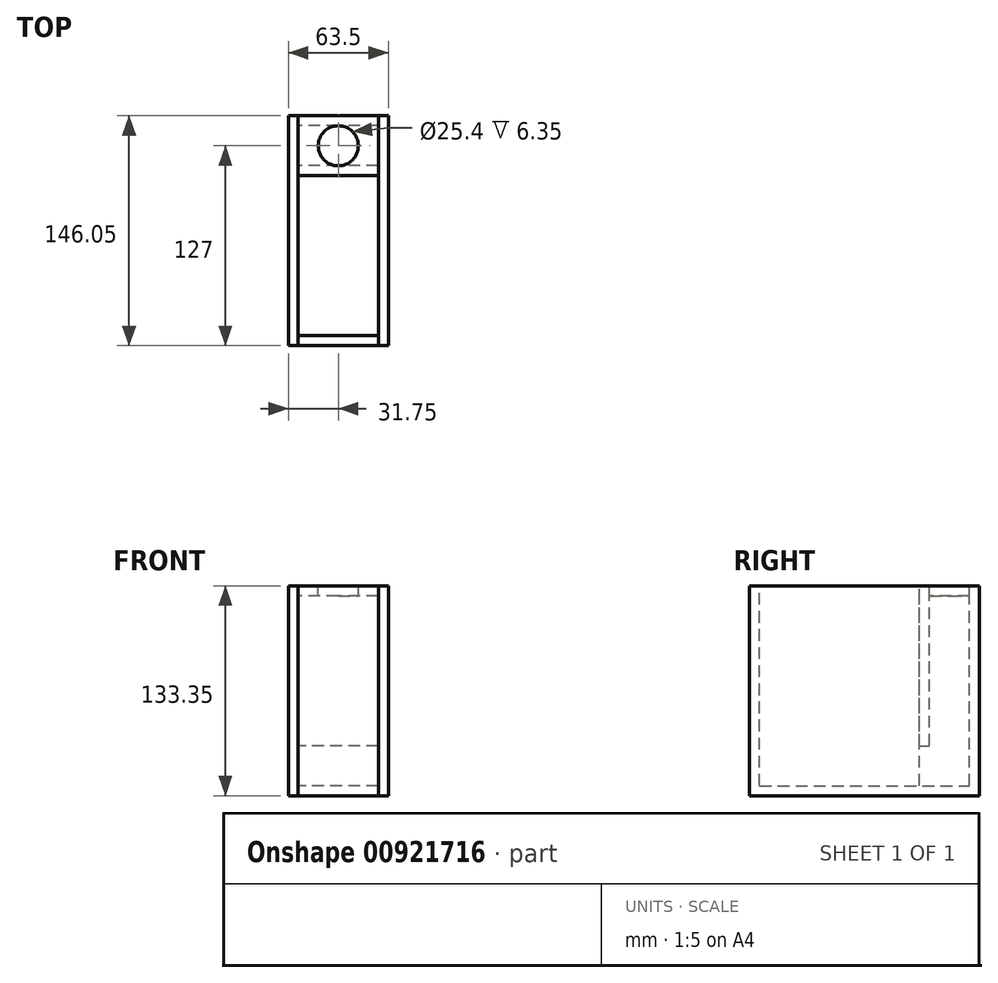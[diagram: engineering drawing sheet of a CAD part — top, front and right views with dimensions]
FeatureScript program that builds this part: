
annotation { "Feature Type Name" : "Feature", "Feature Type Description" : "" }
export const myFeature = defineFeature(function(context is Context, id is Id, definition is map)
    precondition{}
    {
        {
            var Q0;
            Q0=qCreatedBy(makeId("Right.planeOp"),FACE);
            var sketch = newSketch(context, id + "F0", { "sketchPlane" : qUnion([Q0])});
            skLineSegment(sketch, "E0.bottom", {"start": v(-50.8, 0) * mm, "end": v(50.8, 0) * mm});
            skLineSegment(sketch, "E0.top", {"start": v(-50.8, 127) * mm, "end": v(50.8, 127) * mm});
            skLineSegment(sketch, "E0.left", {"start": v(-50.8, 0) * mm, "end": v(-50.8, 127) * mm});
            skLineSegment(sketch, "E0.right", {"start": v(50.8, 0) * mm, "end": v(50.8, 127) * mm});
            skPoint(sketch, "E1", {"position": v(0, 0) * mm});
            skSolve(sketch);
        }
        {
            var Q0;
            Q0 = qSketchRegion(id + "F0", true);
            extrude(context, id + "F1", {"entities" : qUnion([Q0]), "oppositeDirection" : true, "depth" : 50.8 * mm, "offsetDistance" : 25.4 * mm});
        }
        {
            var Q0;
            Q0=makeQuery(id+"F1.opExtrude","CAP_FACE",FACE,{"disambiguationData":[OSD([sQuery(id+"F0.wireOp",EDGE,"E0.bottom"),sQuery(id+"F0.wireOp",EDGE,"E0.top"),sQuery(id+"F0.wireOp",EDGE,"E0.left"),sQuery(id+"F0.wireOp",EDGE,"E0.right")])],"isStart":false});
            var sketch = newSketch(context, id + "F2", { "sketchPlane" : qUnion([Q0])});
            skLineSegment(sketch, "E2", {"start": v(50.8, 0) * mm, "end": v(-82.55, 0) * mm});
            skLineSegment(sketch, "E3", {"start": v(-82.55, 0) * mm, "end": v(-82.55, 120.65) * mm});
            skLineSegment(sketch, "E4", {"start": v(-82.55, 120.65) * mm, "end": v(-50.8, 120.65) * mm});
            skLineSegment(sketch, "E5", {"start": v(-50.8, 120.65) * mm, "end": v(-50.8, 25.4) * mm});
            skLineSegment(sketch, "E6", {"start": v(-50.8, 25.4) * mm, "end": v(-57.15, 25.4) * mm});
            skLineSegment(sketch, "E7", {"start": v(-57.15, 25.4) * mm, "end": v(-57.15, 120.65) * mm});
            skLineSegment(sketch, "E8", {"start": v(-50.8, 120.65) * mm, "end": v(-50.8, 127) * mm});
            skLineSegment(sketch, "E9", {"start": v(-50.8, 127) * mm, "end": v(-82.55, 127) * mm});
            skLineSegment(sketch, "E10", {"start": v(-82.55, 127) * mm, "end": v(-88.9, 127) * mm});
            skLineSegment(sketch, "E11", {"start": v(-88.9, 127) * mm, "end": v(-88.9, 0) * mm});
            skLineSegment(sketch, "E12", {"start": v(-88.9, 0) * mm, "end": v(-88.9, -6.35) * mm});
            skLineSegment(sketch, "E13", {"start": v(-88.9, -6.35) * mm, "end": v(57.15, -6.35) * mm});
            skLineSegment(sketch, "E14", {"start": v(57.15, -6.35) * mm, "end": v(57.15, 127) * mm});
            skLineSegment(sketch, "E15", {"start": v(57.15, 127) * mm, "end": v(50.8, 127) * mm});
            skLineSegment(sketch, "E16", {"start": v(50.8, 127) * mm, "end": v(50.8, 0) * mm});
            skLineSegment(sketch, "E17", {"start": v(-57.15, 25.4) * mm, "end": v(-82.55, 0) * mm, "construction": true});
            skSolve(sketch);
        }
        {
            var Q0;
            Q0 = qSketchRegion(id + "F2", true);
            var Q1;
            Q1=makeQuery(id+"F2.imprint","IMPRINT",FACE,{"disambiguationData":[TD([[makeQuery(id+"F2.imprint","IMPRINT",EDGE,{"derivedFrom":sQuery(id+"F2.wireOp",EDGE,"A4J26bFV-rywj-hipJ-cBjO-Lqcr4Hk2ZQzP.bottom")}),1.0]])]});
            var Q2;
            Q2=makeQuery(id+"F1.opExtrude","CAP_FACE",FACE,{"disambiguationData":[OSD([sQuery(id+"F0.wireOp",EDGE,"E0.bottom"),sQuery(id+"F0.wireOp",EDGE,"E0.top"),sQuery(id+"F0.wireOp",EDGE,"E0.left"),sQuery(id+"F0.wireOp",EDGE,"E0.right")])],"isStart":true});
            extrude(context, id + "F3", {"entities" : qUnion([Q0, Q1]), "endBound" : BoundingType.UP_TO_SURFACE, "oppositeDirection" : true, "depth" : 25.4 * mm, "endBoundEntityFace" : qUnion([Q2]), "offsetDistance" : 25.4 * mm});
        }
        {
            var Q0;
            Q0=makeQuery(id+"F3.opExtrude","CAP_FACE",FACE,{"disambiguationData":[OSD([sQuery(id+"F2.wireOp",EDGE,"E2"),sQuery(id+"F2.wireOp",EDGE,"E3"),sQuery(id+"F2.wireOp",EDGE,"E4"),sQuery(id+"F2.wireOp",EDGE,"E5"),sQuery(id+"F2.wireOp",EDGE,"E6"),sQuery(id+"F2.wireOp",EDGE,"E7"),sQuery(id+"F2.wireOp",EDGE,"E8"),sQuery(id+"F2.wireOp",EDGE,"E9"),sQuery(id+"F2.wireOp",EDGE,"E10"),sQuery(id+"F2.wireOp",EDGE,"E11"),sQuery(id+"F2.wireOp",EDGE,"E12"),sQuery(id+"F2.wireOp",EDGE,"E13"),sQuery(id+"F2.wireOp",EDGE,"E14"),sQuery(id+"F2.wireOp",EDGE,"E15"),sQuery(id+"F2.wireOp",EDGE,"E16")])],"isStart":true});
            var sketch = newSketch(context, id + "F4", { "sketchPlane" : qUnion([Q0])});
            skLineSegment(sketch, "E18.bottom", {"start": v(-88.9, 127) * mm, "end": v(57.15, 127) * mm});
            skLineSegment(sketch, "E18.top", {"start": v(-88.9, -6.35) * mm, "end": v(57.15, -6.35) * mm});
            skLineSegment(sketch, "E18.left", {"start": v(-88.9, 127) * mm, "end": v(-88.9, -6.35) * mm});
            skLineSegment(sketch, "E18.right", {"start": v(57.15, 127) * mm, "end": v(57.15, -6.35) * mm});
            skSolve(sketch);
        }
        {
            var Q0;
            Q0 = qSketchRegion(id + "F4", true);
            var Q1;
            {var subQ1=sQuery(id+"F2.wireOp",EDGE,"OunrTzoC-Ow74-cI66-Frwy-KkpsYNKgRBLo.left");Q1=makeQuery(id+"F4.imprint","IMPRINT",FACE,{"disambiguationData":[TD([[makeQuery(id+"F4.imprint","IMPRINT",EDGE,{"derivedFrom":makeQuery(id+"F3.opExtrude","CAP_EDGE",EDGE,{"disambiguationData":[OSD([subQ1])],"isStart":false})}),1.0]])]});}
            var Q2;
            {var subQ4=sQuery(id+"F2.wireOp",EDGE,"OunrTzoC-Ow74-cI66-Frwy-KkpsYNKgRBLo.left");Q2=makeQuery(id+"F4.imprint","IMPRINT",FACE,{"disambiguationData":[TD([[makeQuery(id+"F4.imprint","IMPRINT",EDGE,{"derivedFrom":makeQuery(id+"F3.opExtrude","CAP_EDGE",EDGE,{"disambiguationData":[OSD([subQ4])],"isStart":false})}),-1.0]])]});}
            extrude(context, id + "F5", {"entities" : qUnion([Q0, Q1, Q2]), "depth" : 6.35 * mm, "offsetDistance" : 25.4 * mm});
        }
        {
            var Q0;
            Q0=makeQuery(id+"F3.opExtrude","SWEPT_EDGE",EDGE,{"disambiguationData":[OSD([sQuery(id+"F2.wireOp",EDGE,"E14"),sQuery(id+"F2.wireOp",EDGE,"E15")])]});
            cPoint(context, id + "F6", {"entities" : qUnion([Q0]), "parameter" : 0.5});
        }
        {
            var Q0;
            Q0 = qCreatedBy(id + "F6" ,VERTEX);
            var Q1;
            Q1=makeQuery(id+"F5.opExtrude","CAP_FACE",FACE,{"disambiguationData":[OSD([sQuery(id+"F4.wireOp",EDGE,"E18.bottom"),sQuery(id+"F4.wireOp",EDGE,"E18.top"),sQuery(id+"F4.wireOp",EDGE,"E18.left"),sQuery(id+"F4.wireOp",EDGE,"E18.right")])],"isStart":true});
            cPlane(context, id + "F7", {"entities" : qUnion([Q0, Q1]), "cplaneType" : CPlaneType.PLANE_POINT, "offset" : 25.4 * mm, "width" : 152.4 * mm, "height" : 152.4 * mm});
        }
        {
            var Q0;
            Q0=makeQuery(id+"F5.opExtrude","SWEPT_BODY",BODY,{"disambiguationData":[OSD([sQuery(id+"F4.wireOp",EDGE,"E18.bottom"),sQuery(id+"F4.wireOp",EDGE,"E18.top"),sQuery(id+"F4.wireOp",EDGE,"E18.left"),sQuery(id+"F4.wireOp",EDGE,"E18.right")])]});
            var Q1;
            Q1=qCreatedBy(id+"F7.planeOp",FACE);
            mirror(context, id + "F8", {"entities" : qUnion([Q0]), "mirrorPlane" : qUnion([Q1])});
        }
        {
            var Q0;
            Q0=makeQuery(id+"F3.opExtrude","SWEPT_FACE",FACE,{"disambiguationData":[OSD([sQuery(id+"F2.wireOp",EDGE,"E9"),sQuery(id+"F2.wireOp",EDGE,"E10")])]});
            var sketch = newSketch(context, id + "F9", { "sketchPlane" : qUnion([Q0])});
            skLineSegment(sketch, "E19", {"start": v(0, 69.85) * mm, "end": v(-50.8, 69.85) * mm, "construction": true});
            skCircle(sketch, "E20", {"center": v(-25.4, 69.85) * mm, "radius": 12.7 * mm});
            skSolve(sketch);
        }
        {
            var Q0;
            Q0 = qSketchRegion(id + "F9", true);
            extrude(context, id + "F10", {"entities" : qUnion([Q0]), "operationType" : NewBodyOperationType.REMOVE, "oppositeDirection" : true, "depth" : 6.35 * mm, "offsetDistance" : 25.4 * mm});
        }
    });
